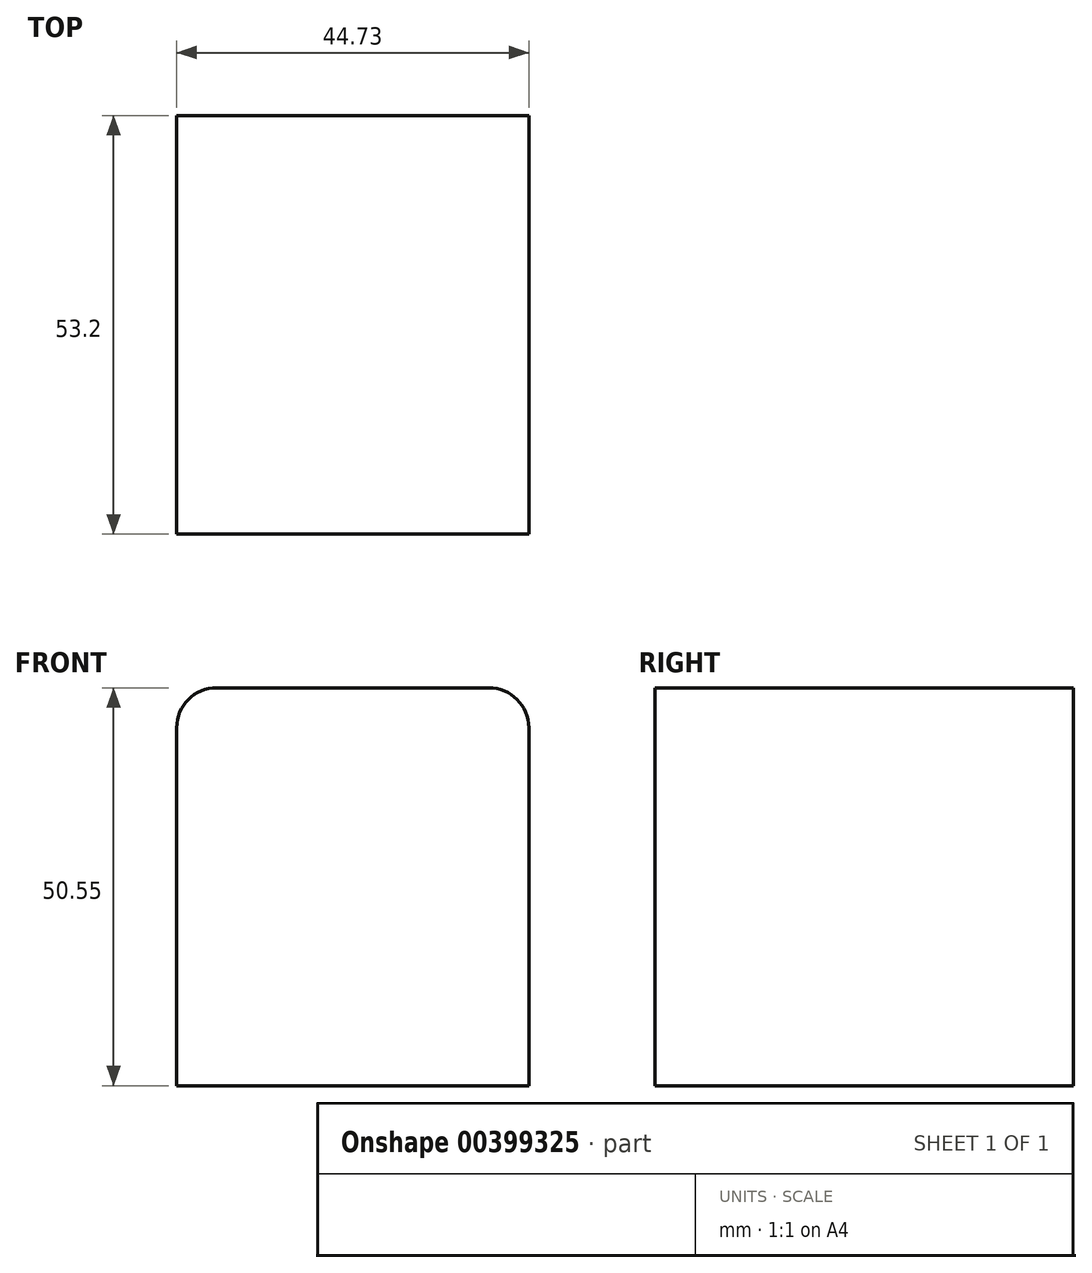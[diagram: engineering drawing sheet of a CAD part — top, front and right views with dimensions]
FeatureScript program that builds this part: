
annotation { "Feature Type Name" : "Feature", "Feature Type Description" : "" }
export const myFeature = defineFeature(function(context is Context, id is Id, definition is map)
    precondition{}
    {
        {
            var Q0;
            Q0=qCreatedBy(makeId("Top.planeOp"),FACE);
            var sketch = newSketch(context, id + "F0", { "sketchPlane" : qUnion([Q0])});
            skLineSegment(sketch, "E0.bottom", {"start": v(0, 0) * mm, "end": v(44.73, 0) * mm});
            skLineSegment(sketch, "E0.top", {"start": v(0, 53.2) * mm, "end": v(44.73, 53.2) * mm});
            skLineSegment(sketch, "E0.left", {"start": v(0, 0) * mm, "end": v(0, 53.2) * mm});
            skLineSegment(sketch, "E0.right", {"start": v(44.73, 0) * mm, "end": v(44.73, 53.2) * mm});
            skSolve(sketch);
        }
        {
            var Q0;
            Q0 = qSketchRegion(id + "F0", true);
            extrude(context, id + "F1", {"entities" : qUnion([Q0]), "depth" : 50.55 * mm});
        }
        {
            var Q0;
            Q0=makeQuery(id+"F1.opExtrude","CAP_EDGE",EDGE,{"disambiguationData":[OSD([sQuery(id+"F0.wireOp",EDGE,"E0.left")])],"isStart":false});
            var Q1;
            Q1=makeQuery(id+"F1.opExtrude","CAP_EDGE",EDGE,{"disambiguationData":[OSD([sQuery(id+"F0.wireOp",EDGE,"E0.right")])],"isStart":false});
            fillet(context, id + "F2", {"entities" : qUnion([Q0, Q1]), "radius" : 5.08 * mm, "tangentPropagation" : true, "allowEdgeOverflow" : false});
        }
    });
